# Revit family: CENTUM Schutzkappen XL80 - XL120 Logo Grau
name_source: partatom
category: HLS-Bauteile
units: mm (PartAtom-declared; Revit-internal decimal feet)

## family parameters
Arbeitsebenenbasiert = Ja
Beim Laden mit Abzugskörper schneiden = Nein
Bemaßung runder Anschluss = Durchmesser verwenden
Beschriftungsausrichtung beibehalten = Nein
Gemeinsam genutzt = Ja
Immer vertikal = Nein
Raumberechnungspunkt = Nein
Teiletyp = Normal

## types (3) — shared parameters
Fabrikat = MEFA
Farbe = Schwarz
Firma = MEFA Befestigungs- und Montagesysteme GmbH
Kurztext1 = Schutzkappe CENTUM
L1 = 5 mm  [stored 0.0164042 ft]
Material = Kunststoff
Materialname = PE
Mengeneinheit = St
Vorgabe-Ansicht = 1219 mm
vpe = 20

## per-type parameters (varying)
| type | Artikelnummer | B | B1 | B2 | BP | EAN | Gewicht | Gewicht pro Bauteil | H1 | H2 | Kurztext2 | L2 | Profiltyp |
| CENTUM Schutzkappe XL 80 | 1670081 | 80 mm  [stored 0.262467 ft] | 80 mm  [stored 0.262467 ft] | 7 mm  [stored 0.0229659 ft] | 7 mm  [stored 0.0229659 ft] | 4250928463265 | 0.06 kg | 0.06 kg | 13 mm  [stored 0.0426509 ft] | 37 mm  [stored 0.121391 ft] | für Profil XL 80 PE Schwarz | 28 mm | XL 80 |
| CENTUM Schutzkappe XL100 | 1670101 | 100 mm  [stored 0.328084 ft] | 100 mm  [stored 0.328084 ft] | 8 mm  [stored 0.0262467 ft] | 8 mm  [stored 0.0262467 ft] | 4250928463272 | 0.08 kg | 0.08 kg | 22 mm  [stored 0.0721785 ft] | 46 mm  [stored 0.150919 ft] | für Profil XL 100 PE Schwarz | 27 mm  [stored 0.0885827 ft] | XL 100 |
| CENTUM Schutzkappe XL120 | 1670121 | 100 mm  [stored 0.328084 ft] | 120 mm  [stored 0.393701 ft] | 8 mm  [stored 0.0262467 ft] | 9 mm  [stored 0.0295276 ft] | 4250928463432 | 0.09 kg | 0.09 kg | 27 mm  [stored 0.0885827 ft] | 56 mm  [stored 0.183727 ft] | für Profil XL 120 PE Schwarz | 27 mm  [stored 0.0885827 ft] | XL 120 |

note: [stored X ft] marks values corroborated as IEEE doubles in the binary element streams (Revit-internal decimal feet)
